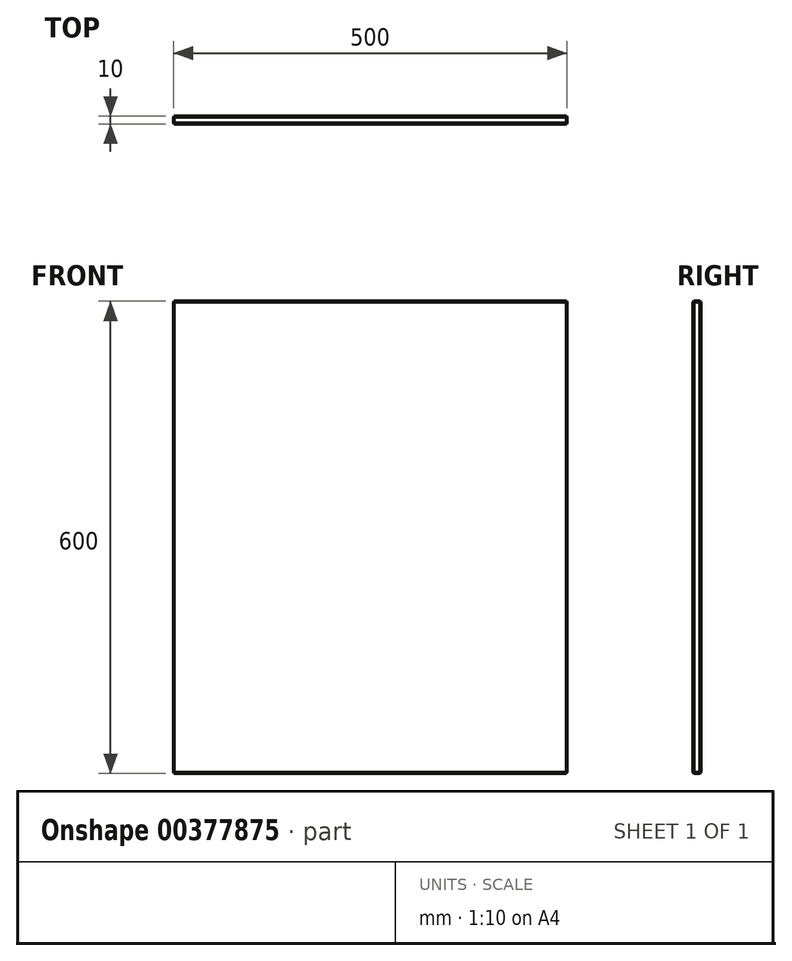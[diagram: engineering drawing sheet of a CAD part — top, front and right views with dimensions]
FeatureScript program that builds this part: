
annotation { "Feature Type Name" : "Feature", "Feature Type Description" : "" }
export const myFeature = defineFeature(function(context is Context, id is Id, definition is map)
    precondition{}
    {
        {
            var Q0;
            Q0=qCreatedBy(makeId("Front.planeOp"),FACE);
            var sketch = newSketch(context, id + "F0", { "sketchPlane" : qUnion([Q0])});
            skLineSegment(sketch, "E0.bottom", {"start": v(250, 300) * mm, "end": v(-250, 300) * mm});
            skLineSegment(sketch, "E0.top", {"start": v(250, -300) * mm, "end": v(-250, -300) * mm});
            skLineSegment(sketch, "E0.left", {"start": v(250, 300) * mm, "end": v(250, -300) * mm});
            skLineSegment(sketch, "E0.right", {"start": v(-250, 300) * mm, "end": v(-250, -300) * mm});
            skPoint(sketch, "E0.middle", {"position": v(0, 0) * mm});
            skSolve(sketch);
        }
        {
            var Q0;
            Q0=makeQuery(id+"F0.imprint","IMPRINT",FACE,{"disambiguationData":[TD([[makeQuery(id+"F0.imprint","IMPRINT",EDGE,{"derivedFrom":sQuery(id+"F0.wireOp",EDGE,"E0.bottom")}),1.0]])]});
            extrude(context, id + "F1", {"entities" : qUnion([Q0]), "depth" : 10 * mm});
        }
        {
            var Q0;
            Q0=makeQuery(id+"F1.opExtrude","CAP_EDGE",EDGE,{"disambiguationData":[OSD([sQuery(id+"F0.wireOp",EDGE,"E0.bottom")])],"isStart":false});
            var Q1;
            Q1=makeQuery(id+"F1.opExtrude","CAP_EDGE",EDGE,{"disambiguationData":[OSD([sQuery(id+"F0.wireOp",EDGE,"E0.bottom")])],"isStart":true});
            var Q2;
            Q2=makeQuery(id+"F1.opExtrude","SWEPT_EDGE",EDGE,{"disambiguationData":[OSD([sQuery(id+"F0.wireOp",EDGE,"E0.bottom"),sQuery(id+"F0.wireOp",EDGE,"E0.left")])]});
            var Q3;
            Q3=makeQuery(id+"F1.opExtrude","CAP_EDGE",EDGE,{"disambiguationData":[OSD([sQuery(id+"F0.wireOp",EDGE,"E0.left")])],"isStart":true});
            var Q4;
            Q4=makeQuery(id+"F1.opExtrude","CAP_EDGE",EDGE,{"disambiguationData":[OSD([sQuery(id+"F0.wireOp",EDGE,"E0.left")])],"isStart":false});
            chamfer(context, id + "F2", {"entities" : qUnion([Q0, Q1, Q2, Q3, Q4]), "width" : 1 * mm, "tangentPropagation" : true});
        }
        {
            var Q0;
            Q0=makeQuery(id+"F1.opExtrude","SWEPT_EDGE",EDGE,{"disambiguationData":[OSD([sQuery(id+"F0.wireOp",EDGE,"E0.bottom"),sQuery(id+"F0.wireOp",EDGE,"E0.right")])]});
            var Q1;
            Q1=makeQuery(id+"F1.opExtrude","CAP_EDGE",EDGE,{"disambiguationData":[OSD([sQuery(id+"F0.wireOp",EDGE,"E0.right")])],"isStart":false});
            var Q2;
            Q2=makeQuery(id+"F1.opExtrude","CAP_EDGE",EDGE,{"disambiguationData":[OSD([sQuery(id+"F0.wireOp",EDGE,"E0.right")])],"isStart":true});
            chamfer(context, id + "F3", {"entities" : qUnion([Q0, Q1, Q2]), "width" : 1 * mm, "tangentPropagation" : true});
        }
        {
            var Q0;
            Q0=makeQuery(id+"F1.opExtrude","SWEPT_EDGE",EDGE,{"disambiguationData":[OSD([sQuery(id+"F0.wireOp",EDGE,"E0.top"),sQuery(id+"F0.wireOp",EDGE,"E0.left")])]});
            var Q1;
            Q1=makeQuery(id+"F1.opExtrude","CAP_EDGE",EDGE,{"disambiguationData":[OSD([sQuery(id+"F0.wireOp",EDGE,"E0.top")])],"isStart":false});
            var Q2;
            Q2=makeQuery(id+"F1.opExtrude","CAP_EDGE",EDGE,{"disambiguationData":[OSD([sQuery(id+"F0.wireOp",EDGE,"E0.top")])],"isStart":true});
            var Q3;
            Q3=makeQuery(id+"F1.opExtrude","SWEPT_EDGE",EDGE,{"disambiguationData":[OSD([sQuery(id+"F0.wireOp",EDGE,"E0.top"),sQuery(id+"F0.wireOp",EDGE,"E0.right")])]});
            chamfer(context, id + "F4", {"entities" : qUnion([Q0, Q1, Q2, Q3]), "width" : 1 * mm, "tangentPropagation" : true});
        }
    });
